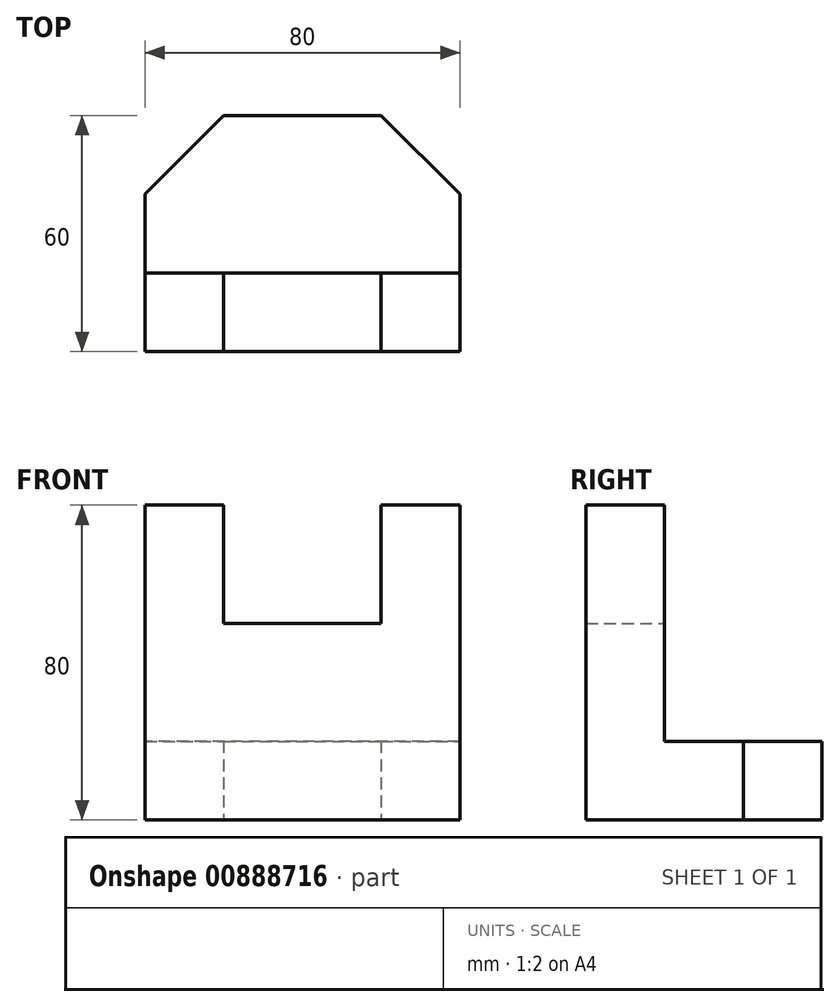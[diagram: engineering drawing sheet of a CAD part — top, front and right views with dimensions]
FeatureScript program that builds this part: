
annotation { "Feature Type Name" : "Feature", "Feature Type Description" : "" }
export const myFeature = defineFeature(function(context is Context, id is Id, definition is map)
    precondition{}
    {
        {
            var Q0;
            Q0=qCreatedBy(makeId("Front.planeOp"),FACE);
            var sketch = newSketch(context, id + "F0", { "sketchPlane" : qUnion([Q0])});
            skLineSegment(sketch, "E0.bottom", {"start": v(-60, 50) * mm, "end": v(-20, 50) * mm});
            skLineSegment(sketch, "E0.top", {"start": v(-80, 0) * mm, "end": v(0, 0) * mm});
            skLineSegment(sketch, "E0.left", {"start": v(-80, 50) * mm, "end": v(-80, 0) * mm});
            skLineSegment(sketch, "E0.right", {"start": v(0, 50) * mm, "end": v(0, 0) * mm});
            skLineSegment(sketch, "E1.top", {"start": v(-80, 80) * mm, "end": v(-60, 80) * mm});
            skLineSegment(sketch, "E1.left", {"start": v(-80, 50) * mm, "end": v(-80, 80) * mm});
            skLineSegment(sketch, "E1.right", {"start": v(-60, 50) * mm, "end": v(-60, 80) * mm});
            skLineSegment(sketch, "E2.top", {"start": v(0, 80) * mm, "end": v(-20, 80) * mm});
            skLineSegment(sketch, "E2.left", {"start": v(0, 50) * mm, "end": v(0, 80) * mm});
            skLineSegment(sketch, "E2.right", {"start": v(-20, 50) * mm, "end": v(-20, 80) * mm});
            skSolve(sketch);
        }
        {
            var Q0;
            Q0=makeQuery(id+"F0.imprint","IMPRINT",FACE,{"disambiguationData":[TD([[makeQuery(id+"F0.imprint","IMPRINT",EDGE,{"derivedFrom":sQuery(id+"F0.wireOp",EDGE,"E0.bottom")}),-1.0]])]});
            extrude(context, id + "F1", {"entities" : qUnion([Q0]), "depth" : 20 * mm, "offsetDistance" : 25 * mm});
        }
        {
            var Q0;
            Q0=qCreatedBy(makeId("Top.planeOp"),FACE);
            var sketch = newSketch(context, id + "F2", { "sketchPlane" : qUnion([Q0])});
            skLineSegment(sketch, "E3.bottom", {"start": v(0, 0) * mm, "end": v(-80, 0) * mm});
            skLineSegment(sketch, "E3.left", {"start": v(0, 0) * mm, "end": v(0, 20) * mm});
            skLineSegment(sketch, "E3.right", {"start": v(-80, 0) * mm, "end": v(-80, 20) * mm});
            skLineSegment(sketch, "E4", {"start": v(-80, 20) * mm, "end": v(-60, 40) * mm});
            skLineSegment(sketch, "E5", {"start": v(-60, 40) * mm, "end": v(-20, 40) * mm});
            skLineSegment(sketch, "E6", {"start": v(-20, 40) * mm, "end": v(0, 20) * mm});
            skSolve(sketch);
        }
        {
            var Q0;
            Q0=makeQuery(id+"F2.imprint","IMPRINT",FACE,{"disambiguationData":[TD([[makeQuery(id+"F2.imprint","IMPRINT",EDGE,{"derivedFrom":sQuery(id+"F2.wireOp",EDGE,"E3.bottom")}),-1.0]])]});
            extrude(context, id + "F3", {"entities" : qUnion([Q0]), "operationType" : NewBodyOperationType.ADD, "depth" : 20 * mm, "offsetDistance" : 25 * mm});
        }
    });
